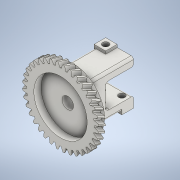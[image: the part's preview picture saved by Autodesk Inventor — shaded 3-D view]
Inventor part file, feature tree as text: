
AUTODESK INVENTOR PART (.ipt)
format: ipt  version: 2022 (Build 260153070, 153G)  size: 723,456 bytes
history: native  units: mm (DEFAULTED — no unit token found)
features: extrude x9, sketch x8, plane x4, other x4, fillet x4, pattern_circular x1, loft x1
ambient origin geometry x8: Origin, YZ Plane, XZ Plane, XY Plane, X Axis, Y Axis, Z Axis, Center Point
bodies: Solid1 (feature_tree)
feature tree (31):
  extrude  "Extrusion1"  Depth=3.0mm TaperAngle=0.0deg
  plane  "Work Plane2"
  plane  "Work Plane8"
  plane  "Work Plane9"
  other  "Spur Gear"
  sketch  "Sketch4"  dims[d41=0.0mm d43=20.0mm]
  extrude  "Extrusion3"  Depth=10.0mm TaperAngle=0.0deg
  fillet  "Fillet1"  Radius=20.0mm
  sketch  "Sketch6"  dims[d49=23.05mm d50=0.15mm d51=0.0mm d52=27.0mm]
  extrude  "Extrusion5"  TaperAngle=0.0deg  [1 undecoded]
  extrude  "Extrusion6"  Depth=20.0mm
  extrude  "Extrusion2"  TaperAngle=0.0deg  [1 undecoded]
  extrude  "Extrusion4"  Depth=0.15mm TaperAngle=0.0deg
  fillet  "Fillet2"  Radius=27.0mm
  sketch  "Sketch7"  dims[d53=5.0mm d54=0.0mm d55=2.5mm d56=0.0mm]
  extrude  "Extrusion7"  Depth=2.5mm TaperAngle=0.0deg
  extrude  "Extrusion8"  Depth=1.0mm
  pattern_circular  "Circular Pattern1"  Count=2  [1 undecoded]
  fillet  "Fillet3"  Radius=12.0mm
  plane  "Work Plane11"
  sketch  "Sketch8"  dims[d57=1.0mm d58=5.0mm d59=20.0mm d60=0.0mm d63=12.0mm d64=18.0mm d65=3.5mm d66=3.5mm d67=20.0mm d68=0.0mm d69=5.0mm d70=0.0mm d71=1.0mm d72=5.0mm d73=5.0mm d74=2.7mm d75=2.5mm d76=2.5mm d77=1.2mm d78=0.0mm d79=3.5mm d80=0.0mm d81=20.0mm d82=360.0deg d84=1.0mm d85=3.75mm d86=0.0mm d87=90.0deg d88=0.0mm d89=90.0deg d90=3.5mm d91=0.0mm d92=1.0mm]
  extrude  "Extrusion9"  Depth=1.0mm
  loft  "Loft1"
  fillet  "Fillet4"  Radius=3.5mm
  sketch  "Sketch1"  dims[d0=32.839078mm d1=3.0mm d2=0.0mm]
  sketch  "Sketch2"  dims[d3=31.777284mm d4=10.0mm d5=0.0mm d16=20.0mm]
  other  "Srf1"
  sketch  "Sketch3"  dims[d17=0.0mm d34=0.872665mm d39=0.0mm]
  sketch  "Sketch5"  dims[d46=20.0mm d47=0.0mm d48=0.0mm]
  other  "Edges1"
  other  "Pitch Diameter"
note: 3 required parameter values undecoded (feature->parameter linkage not recoverable at this tier; creation-order binding heuristic only, values carry confidence <= 0.55)
